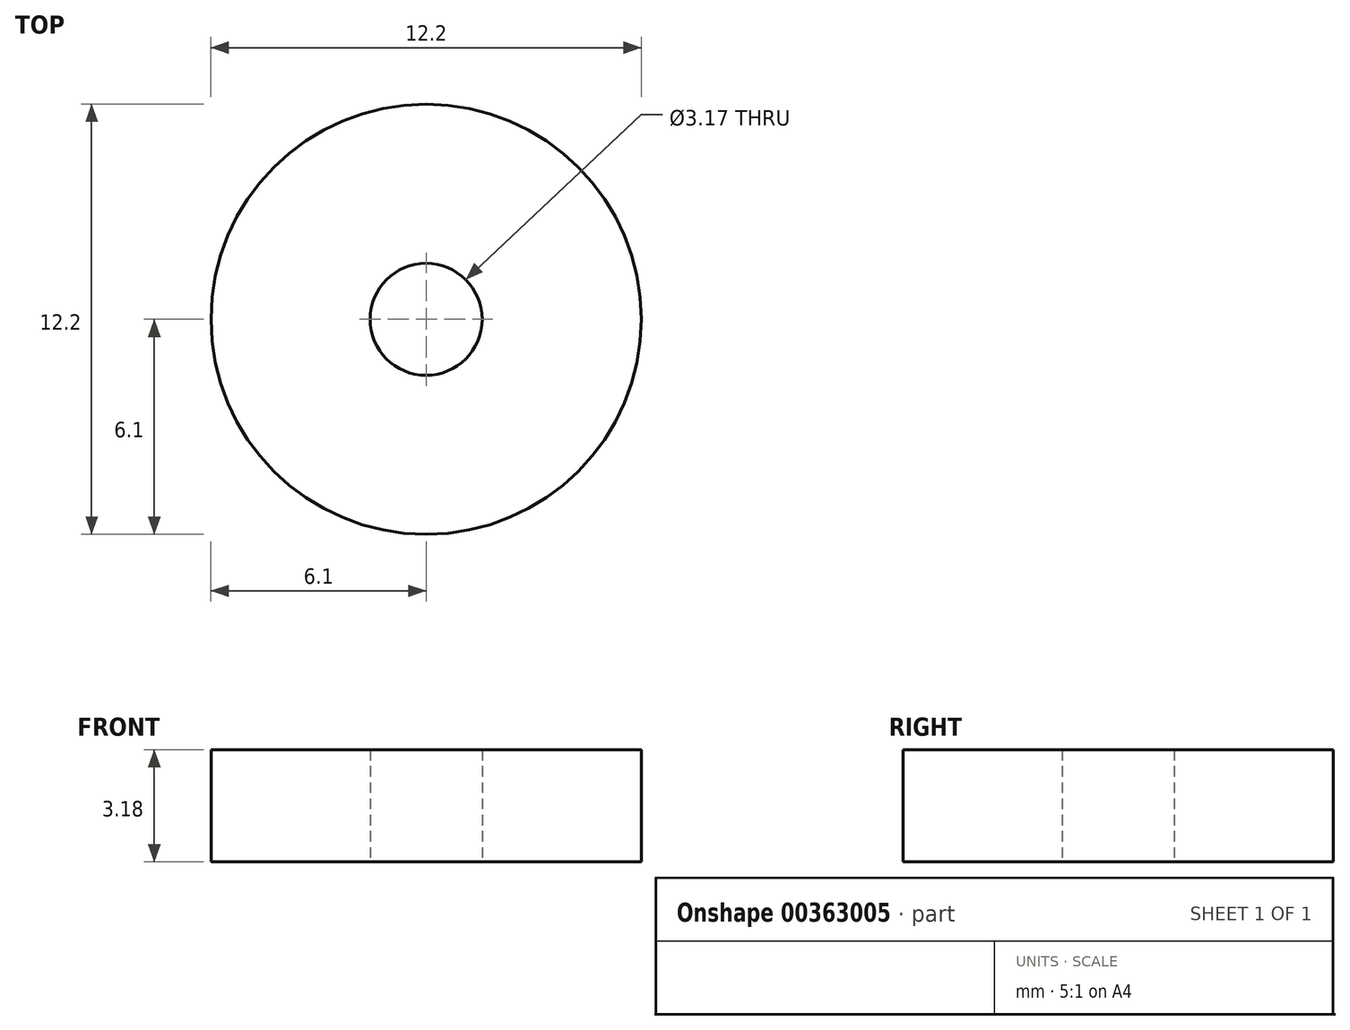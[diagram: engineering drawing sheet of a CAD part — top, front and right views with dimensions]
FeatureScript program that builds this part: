
annotation { "Feature Type Name" : "Feature", "Feature Type Description" : "" }
export const myFeature = defineFeature(function(context is Context, id is Id, definition is map)
    precondition{}
    {
        {
            var Q0;
            Q0=qCreatedBy(makeId("Top.planeOp"),FACE);
            var sketch = newSketch(context, id + "F0", { "sketchPlane" : qUnion([Q0])});
            skCircle(sketch, "E0", {"center": v(0, 0) * mm, "radius": 6.1 * mm});
            skCircle(sketch, "E1", {"center": v(0, 0) * mm, "radius": 1.59 * mm});
            skSolve(sketch);
        }
        {
            var Q0;
            Q0=makeQuery(id+"F0.imprint","IMPRINT",FACE,{"disambiguationData":[TD([[makeQuery(id+"F0.imprint","IMPRINT",EDGE,{"derivedFrom":sQuery(id+"F0.wireOp",EDGE,"E0")}),1.0]])]});
            extrude(context, id + "F1", {"entities" : qUnion([Q0]), "depth" : 3.17 * mm});
        }
    });
